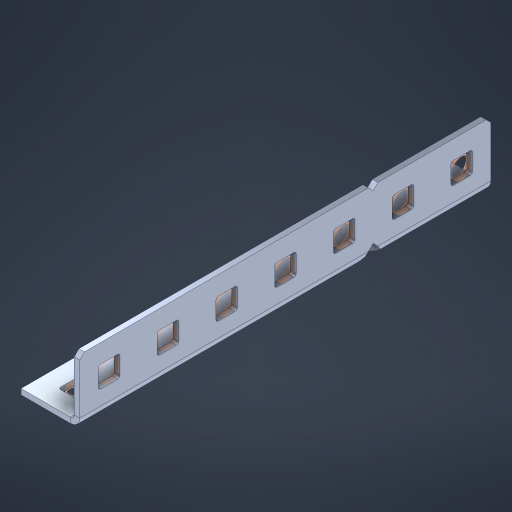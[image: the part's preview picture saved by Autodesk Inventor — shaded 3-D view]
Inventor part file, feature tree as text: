
AUTODESK INVENTOR PART (.ipt)
format: ipt  version: 2023 (Build 270158000, 158)  size: 492,032 bytes
history: native  units: in
note: dims shown in document units (in); Inventor stores cm internally (conversion verified against a paired STEP export)
features: other x19, extrude x13, sheet_metal_op x10, sketch x8, mirror x1, pattern_linear x1, chamfer x1
ambient origin geometry x8: Origin, YZ Plane, XZ Plane, XY Plane, X Axis, Y Axis, Z Axis, Center Point
bodies: Solid1 (feature_tree), Body (feature_tree)
feature tree (53):
  other  "Flange Pattern Plane"
  sheet_metal_op  "Flange Pattern"
  sheet_metal_op  "Body Pattern"
  other  "Arc Length"
  mirror  "Notch Mirror"
  pattern_linear  "Notch Pattern"  Spacing1=0.1875in  [1 undecoded]
  chamfer  "End Chamfer"
  extrude  "Half Cut"  Depth=0.0469in
  sketch  "Sketch1"  dims[d0=2.5in]
  other  "Plate1"
  sketch  "Sketch2"  dims[d1=3.5in]
  other  "Plate2"
  sheet_metal_op  "Bend1"
  sheet_metal_op  "Corner1"
  sketch  "Sketch3"  dims[d2=0.0469in]
  other  "Flange Pattern Sketch"
  sketch  "Sketch7"  dims[d3=0.0469in]
  other  "Srf1"
  other  "Srf2"
  sketch  "Sketch8"  dims[d4=0.0234in]
  sketch  "Sketch9"  dims[d5=0.0938in]
  other  "Srf91"
  sheet_metal_op  "Body Pattern Sketch"
  other  "Srf92"
  sketch  "Sketch13"  dims[d6=0.0469in]
  sketch  "Sketch14"  dims[d7=0.5in d8=90.0deg d9=0.0312in d10=0.1875in d11=0.0469in d12=0.0469in d16=0.182in d17=0.02in d18=0.0469in d19=0.0in d20=0.25in d21=0.25in d46=0.172in d47=1.0in d48=0.0in d49=0.182in d50=0.02in d51=0.25in d52=0.25in d53=0.0469in d54=0.0in d55=0.172in d56=1.0in d57=0.0in d60=2.7559in d62=0.5in d63=0.3937in d65=0.5in d85=0.1227in d86=0.1659in d88=0.04in d89=0.0469in d90=0.0in d91=0.04in d92=0.0491in d95=2.5in d96=0.04in d97=0.25in d98=45.0deg d101=0.0in d102=2.497in d131=0.5in d132=2.7559in d134=0.5in d139=0.5in]
  other  "Srf856"
  other  "Srf1310"
  other  "Srf1311"
  other  "Srf1312"
  other  "Srf1376"
  other  "Srf1377"
  other  "Srf1728"
  other  "Srf1755"
  other  "Srf1878"
  other  "Srf1942"
  sheet_metal_op  "Flange Stamp"
  sheet_metal_op  "Flange Circle"
  sheet_metal_op  "Body Stamp"
  sheet_metal_op  "Body Circle"
  sheet_metal_op  "Notch"
  extrude  "ExtrusionSrf2"  Depth=0.0469in
  extrude  "ExtrusionSrf92"  Depth=0.5in
  extrude  "ExtrusionSrf856"  Depth=0.02in
  extrude  "ExtrusionSrf1310"  Depth=0.0469in
  extrude  "ExtrusionSrf1311"  TaperAngle=0.0deg  [1 undecoded]
  extrude  "ExtrusionSrf1312"  Depth=0.5in
  extrude  "ExtrusionSrf1376"  Depth=0.5in
  extrude  "ExtrusionSrf1377"  Depth=0.5in
  extrude  "ExtrusionSrf1728"  Depth=0.5in TaperAngle=0.0deg
  extrude  "ExtrusionSrf1755"  Depth=0.5in
  extrude  "ExtrusionSrf1878"  Depth=0.02in
  extrude  "ExtrusionSrf1942"  Depth=0.5in
note: 2 required parameter values undecoded (feature->parameter linkage not recoverable at this tier; creation-order binding heuristic only, values carry confidence <= 0.55)
